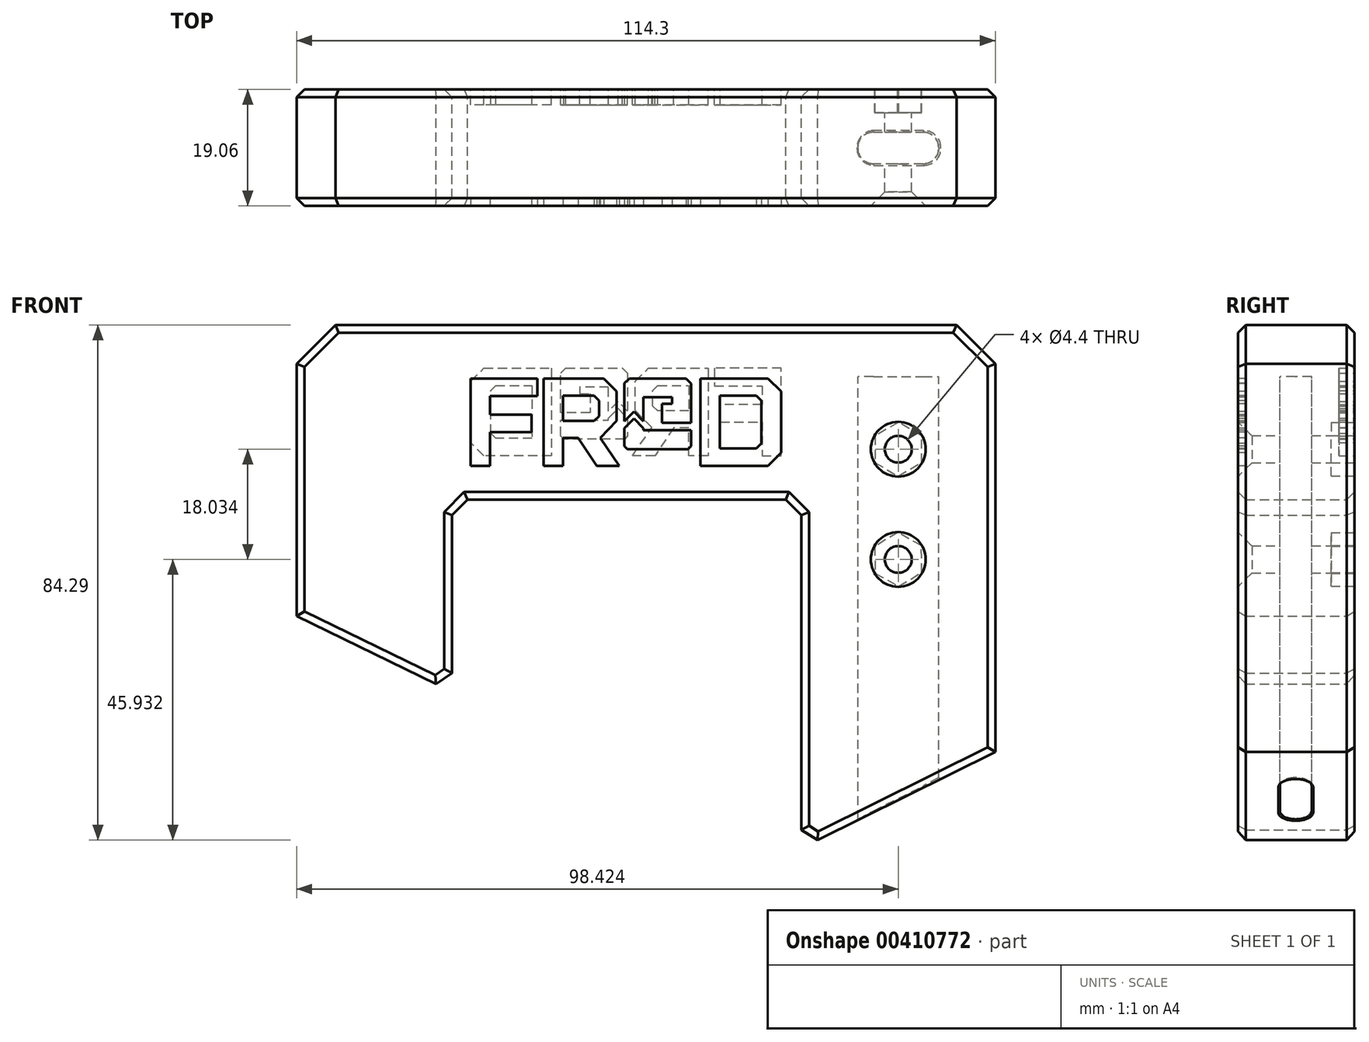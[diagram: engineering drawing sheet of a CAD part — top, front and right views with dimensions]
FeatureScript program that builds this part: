
annotation { "Feature Type Name" : "Feature", "Feature Type Description" : "" }
export const myFeature = defineFeature(function(context is Context, id is Id, definition is map)
    precondition{}
    {
        {
            var Q0;
            Q0=qCreatedBy(makeId("Front.planeOp"),FACE);
            var sketch = newSketch(context, id + "F0", { "sketchPlane" : qUnion([Q0])});
            skLineSegment(sketch, "E0", {"start": v(-47.53, 34.12) * mm, "end": v(54.07, 34.12) * mm});
            skLineSegment(sketch, "E1", {"start": v(60.42, 27.77) * mm, "end": v(60.42, -35.73) * mm});
            skLineSegment(sketch, "E2", {"start": v(60.42, -35.73) * mm, "end": v(31.37, -50.17) * mm});
            skLineSegment(sketch, "E3", {"start": v(28.67, -48.5) * mm, "end": v(28.67, 3) * mm});
            skLineSegment(sketch, "E4", {"start": v(26.13, 5.54) * mm, "end": v(-25.94, 5.54) * mm});
            skLineSegment(sketch, "E5", {"start": v(-28.48, 3) * mm, "end": v(-28.48, -22.82) * mm});
            skLineSegment(sketch, "E6", {"start": v(-31.1, -24.62) * mm, "end": v(-53.88, -13.5) * mm});
            skLineSegment(sketch, "E7", {"start": v(-53.88, -13.5) * mm, "end": v(-53.88, 27.77) * mm});
            skLineSegment(sketch, "E8", {"start": v(-31.1, -24.62) * mm, "end": v(-28.48, -22.82) * mm});
            skLineSegment(sketch, "E9", {"start": v(28.67, -48.5) * mm, "end": v(31.37, -50.17) * mm});
            skLineSegment(sketch, "E10", {"start": v(-53.88, 27.77) * mm, "end": v(-47.53, 34.12) * mm});
            skPoint(sketch, "E11.orphan", {"position": v(-53.88, 34.12) * mm});
            skLineSegment(sketch, "E12", {"start": v(54.07, 34.12) * mm, "end": v(60.42, 27.77) * mm});
            skPoint(sketch, "E13.orphan", {"position": v(60.42, 34.12) * mm});
            skLineSegment(sketch, "E14", {"start": v(-28.48, 3) * mm, "end": v(-25.94, 5.54) * mm});
            skPoint(sketch, "E15.orphan", {"position": v(-28.48, 5.54) * mm});
            skLineSegment(sketch, "E16", {"start": v(26.13, 5.54) * mm, "end": v(28.67, 3) * mm});
            skPoint(sketch, "E17.orphan", {"position": v(28.67, 5.54) * mm});
            skSolve(sketch);
        }
        {
            var Q0;
            Q0=makeQuery(id+"F0.imprint","IMPRINT",FACE,{"disambiguationData":[TD([[makeQuery(id+"F0.imprint","IMPRINT",EDGE,{"derivedFrom":sQuery(id+"F0.wireOp",EDGE,"E0")}),-1.0]])]});
            var Q1;
            Q1=makeQuery(id+"F0.imprint","IMPRINT",FACE,{"disambiguationData":[TD([[makeQuery(id+"F0.imprint","IMPRINT",EDGE,{"derivedFrom":sQuery(id+"F0.wireOp",EDGE,"ZEpFWphL-ozMd-Qc4S-y12z-fugVZn2PExex")}),1.0]])]});
            var Q2;
            Q2=makeQuery(id+"F0.imprint","IMPRINT",FACE,{"disambiguationData":[TD([[makeQuery(id+"F0.imprint","IMPRINT",EDGE,{"derivedFrom":sQuery(id+"F0.wireOp",EDGE,"a8f3txKb-fRa5-LG7a-W4z5-OOKFphKNCb56")}),1.0]])]});
            extrude(context, id + "F1", {"entities" : qUnion([Q0, Q1, Q2]), "depth" : 19.05 * mm, "offsetDistance" : 25.4 * mm, "symmetric" : true});
        }
        {
            var Q0;
            Q0=qCreatedBy(makeId("Top.planeOp"),FACE);
            var sketch = newSketch(context, id + "F2", { "sketchPlane" : qUnion([Q0])});
            skLineSegment(sketch, "E18.bottom", {"start": v(40.48, -2.67) * mm, "end": v(48.6, -2.67) * mm});
            skLineSegment(sketch, "E18.top", {"start": v(40.48, 2.54) * mm, "end": v(48.6, 2.54) * mm});
            skLineSegment(sketch, "E18.left", {"start": v(37.94, -0.13) * mm, "end": v(37.94, 0) * mm});
            skLineSegment(sketch, "E18.right", {"start": v(51.15, -0.13) * mm, "end": v(51.15, 0) * mm});
            skPoint(sketch, "E19.visualSharp", {"position": v(37.94, -2.67) * mm});
            skArc(sketch, "E19.filletArc", {"start": v(37.94, -0.13) * mm, "mid": v(38.68, -1.93) * mm, "end": v(40.48, -2.67) * mm});
            skPoint(sketch, "E20.visualSharp", {"position": v(37.94, 2.54) * mm});
            skArc(sketch, "E20.filletArc", {"start": v(40.48, 2.54) * mm, "mid": v(38.68, 1.8) * mm, "end": v(37.94, 0) * mm});
            skPoint(sketch, "E21.visualSharp", {"position": v(51.15, 2.54) * mm});
            skArc(sketch, "E21.filletArc", {"start": v(51.15, 0) * mm, "mid": v(50.4, 1.8) * mm, "end": v(48.6, 2.54) * mm});
            skPoint(sketch, "E22.visualSharp", {"position": v(51.15, -2.67) * mm});
            skArc(sketch, "E22.filletArc", {"start": v(48.6, -2.67) * mm, "mid": v(50.4, -1.93) * mm, "end": v(51.15, -0.13) * mm});
            skSolve(sketch);
        }
        {
            var Q0;
            Q0=makeQuery(id+"F2.imprint","IMPRINT",FACE,{"disambiguationData":[TD([[makeQuery(id+"F2.imprint","IMPRINT",EDGE,{"derivedFrom":sQuery(id+"F2.wireOp",EDGE,"E18.bottom")}),1.0]])]});
            extrude(context, id + "F3", {"entities" : qUnion([Q0]), "operationType" : NewBodyOperationType.REMOVE, "oppositeDirection" : true, "depth" : 59.33 * mm, "offsetDistance" : 25.4 * mm, "hasSecondDirection" : true, "secondDirectionOppositeDirection" : false, "secondDirectionDepth" : 25.65 * mm});
        }
        {
            var Q0;
            Q0=makeQuery(id+"F1.opExtrude","CAP_EDGE",EDGE,{"disambiguationData":[OSD([sQuery(id+"F0.wireOp",EDGE,"E0")])],"isStart":false});
            var Q1;
            Q1=makeQuery(id+"F1.opExtrude","CAP_EDGE",EDGE,{"disambiguationData":[OSD([sQuery(id+"F0.wireOp",EDGE,"E12")])],"isStart":false});
            var Q2;
            Q2=makeQuery(id+"F1.opExtrude","CAP_EDGE",EDGE,{"disambiguationData":[OSD([sQuery(id+"F0.wireOp",EDGE,"E1")])],"isStart":false});
            var Q3;
            Q3=makeQuery(id+"F1.opExtrude","CAP_EDGE",EDGE,{"disambiguationData":[OSD([sQuery(id+"F0.wireOp",EDGE,"E4")])],"isStart":false});
            var Q4;
            Q4=makeQuery(id+"F1.opExtrude","CAP_EDGE",EDGE,{"disambiguationData":[OSD([sQuery(id+"F0.wireOp",EDGE,"E16")])],"isStart":false});
            var Q5;
            Q5=makeQuery(id+"F1.opExtrude","CAP_EDGE",EDGE,{"disambiguationData":[OSD([sQuery(id+"F0.wireOp",EDGE,"E3")])],"isStart":false});
            var Q6;
            Q6=makeQuery(id+"F1.opExtrude","CAP_EDGE",EDGE,{"disambiguationData":[OSD([sQuery(id+"F0.wireOp",EDGE,"E9")])],"isStart":false});
            var Q7;
            Q7=makeQuery(id+"F1.opExtrude","CAP_EDGE",EDGE,{"disambiguationData":[OSD([sQuery(id+"F0.wireOp",EDGE,"E2")])],"isStart":false});
            var Q8;
            Q8=makeQuery(id+"F1.opExtrude","CAP_EDGE",EDGE,{"disambiguationData":[OSD([sQuery(id+"F0.wireOp",EDGE,"E1")])],"isStart":true});
            var Q9;
            Q9=makeQuery(id+"F1.opExtrude","CAP_EDGE",EDGE,{"disambiguationData":[OSD([sQuery(id+"F0.wireOp",EDGE,"E2")])],"isStart":true});
            var Q10;
            Q10=makeQuery(id+"F1.opExtrude","CAP_EDGE",EDGE,{"disambiguationData":[OSD([sQuery(id+"F0.wireOp",EDGE,"E12")])],"isStart":true});
            var Q11;
            Q11=makeQuery(id+"F1.opExtrude","CAP_EDGE",EDGE,{"disambiguationData":[OSD([sQuery(id+"F0.wireOp",EDGE,"E0")])],"isStart":true});
            var Q12;
            Q12=makeQuery(id+"F1.opExtrude","CAP_EDGE",EDGE,{"disambiguationData":[OSD([sQuery(id+"F0.wireOp",EDGE,"E3")])],"isStart":true});
            var Q13;
            Q13=makeQuery(id+"F1.opExtrude","CAP_EDGE",EDGE,{"disambiguationData":[OSD([sQuery(id+"F0.wireOp",EDGE,"E9")])],"isStart":true});
            var Q14;
            Q14=makeQuery(id+"F1.opExtrude","CAP_EDGE",EDGE,{"disambiguationData":[OSD([sQuery(id+"F0.wireOp",EDGE,"E16")])],"isStart":true});
            var Q15;
            Q15=makeQuery(id+"F1.opExtrude","CAP_EDGE",EDGE,{"disambiguationData":[OSD([sQuery(id+"F0.wireOp",EDGE,"E4")])],"isStart":true});
            var Q16;
            Q16=makeQuery(id+"F1.opExtrude","CAP_EDGE",EDGE,{"disambiguationData":[OSD([sQuery(id+"F0.wireOp",EDGE,"E14")])],"isStart":true});
            var Q17;
            Q17=makeQuery(id+"F1.opExtrude","CAP_EDGE",EDGE,{"disambiguationData":[OSD([sQuery(id+"F0.wireOp",EDGE,"E5")])],"isStart":true});
            var Q18;
            Q18=makeQuery(id+"F1.opExtrude","CAP_EDGE",EDGE,{"disambiguationData":[OSD([sQuery(id+"F0.wireOp",EDGE,"E8")])],"isStart":true});
            var Q19;
            Q19=makeQuery(id+"F1.opExtrude","CAP_EDGE",EDGE,{"disambiguationData":[OSD([sQuery(id+"F0.wireOp",EDGE,"E6")])],"isStart":true});
            var Q20;
            Q20=makeQuery(id+"F1.opExtrude","CAP_EDGE",EDGE,{"disambiguationData":[OSD([sQuery(id+"F0.wireOp",EDGE,"E7")])],"isStart":true});
            var Q21;
            Q21=makeQuery(id+"F1.opExtrude","CAP_EDGE",EDGE,{"disambiguationData":[OSD([sQuery(id+"F0.wireOp",EDGE,"E10")])],"isStart":true});
            var Q22;
            Q22=makeQuery(id+"F1.opExtrude","CAP_EDGE",EDGE,{"disambiguationData":[OSD([sQuery(id+"F0.wireOp",EDGE,"E10")])],"isStart":false});
            var Q23;
            Q23=makeQuery(id+"F1.opExtrude","CAP_EDGE",EDGE,{"disambiguationData":[OSD([sQuery(id+"F0.wireOp",EDGE,"E7")])],"isStart":false});
            var Q24;
            Q24=makeQuery(id+"F1.opExtrude","CAP_EDGE",EDGE,{"disambiguationData":[OSD([sQuery(id+"F0.wireOp",EDGE,"E6")])],"isStart":false});
            var Q25;
            Q25=makeQuery(id+"F1.opExtrude","CAP_EDGE",EDGE,{"disambiguationData":[OSD([sQuery(id+"F0.wireOp",EDGE,"E8")])],"isStart":false});
            var Q26;
            Q26=makeQuery(id+"F1.opExtrude","CAP_EDGE",EDGE,{"disambiguationData":[OSD([sQuery(id+"F0.wireOp",EDGE,"E5")])],"isStart":false});
            var Q27;
            Q27=makeQuery(id+"F1.opExtrude","CAP_EDGE",EDGE,{"disambiguationData":[OSD([sQuery(id+"F0.wireOp",EDGE,"E14")])],"isStart":false});
            chamfer(context, id + "F4", {"entities" : qUnion([Q0, Q1, Q2, Q3, Q4, Q5, Q6, Q7, Q8, Q9, Q10, Q11, Q12, Q13, Q14, Q15, Q16, Q17, Q18, Q19, Q20, Q21, Q22, Q23, Q24, Q25, Q26, Q27]), "width" : 1.27 * mm, "tangentPropagation" : true});
        }
        {
            var Q0;
            Q0=makeQuery(id+"F3.boolean.opBoolean","INTERSECT",EDGE,{"derivedFrom":[makeQuery(id+"F1.opExtrude","SWEPT_FACE",FACE,{"disambiguationData":[OSD([sQuery(id+"F0.wireOp",EDGE,"E2")])]}),makeQuery(id+"F3.opExtrude","SWEPT_FACE",FACE,{"disambiguationData":[OSD([sQuery(id+"F2.wireOp",EDGE,"E18.bottom")])]})]});
            chamfer(context, id + "F5", {"entities" : qUnion([Q0]), "width" : 0.25 * mm, "tangentPropagation" : true});
        }
        {
            var Q0;
            Q0=makeQuery(id+"F1.opExtrude","CAP_FACE",FACE,{"disambiguationData":[OSD([sQuery(id+"F0.wireOp",EDGE,"E0"),sQuery(id+"F0.wireOp",EDGE,"E1"),sQuery(id+"F0.wireOp",EDGE,"E2"),sQuery(id+"F0.wireOp",EDGE,"E3"),sQuery(id+"F0.wireOp",EDGE,"E4"),sQuery(id+"F0.wireOp",EDGE,"E5"),sQuery(id+"F0.wireOp",EDGE,"E6"),sQuery(id+"F0.wireOp",EDGE,"E7"),sQuery(id+"F0.wireOp",EDGE,"E8"),sQuery(id+"F0.wireOp",EDGE,"E9"),sQuery(id+"F0.wireOp",EDGE,"E10"),sQuery(id+"F0.wireOp",EDGE,"E12"),sQuery(id+"F0.wireOp",EDGE,"E14"),sQuery(id+"F0.wireOp",EDGE,"E16")])],"isStart":false});
            var sketch = newSketch(context, id + "F6", { "sketchPlane" : qUnion([Q0])});
            skCircle(sketch, "E23", {"center": v(44.54, 13.8) * mm, "radius": 1.9 * mm});
            skCircle(sketch, "E24", {"center": v(44.54, -4.24) * mm, "radius": 1.9 * mm});
            skSolve(sketch);
        }
        {
            var Q0;
            Q0=sQuery(id+"F6.wireOp",VERTEX,"E23.center");
            var Q1;
            Q1=sQuery(id+"F6.wireOp",VERTEX,"E24.center");
            var Q2;
            Q2=makeQuery(id+"F1.opExtrude","SWEPT_BODY",BODY,{"disambiguationData":[OSD([sQuery(id+"F0.wireOp",EDGE,"E0"),sQuery(id+"F0.wireOp",EDGE,"E1"),sQuery(id+"F0.wireOp",EDGE,"E2"),sQuery(id+"F0.wireOp",EDGE,"E3"),sQuery(id+"F0.wireOp",EDGE,"E4"),sQuery(id+"F0.wireOp",EDGE,"E5"),sQuery(id+"F0.wireOp",EDGE,"E6"),sQuery(id+"F0.wireOp",EDGE,"E7"),sQuery(id+"F0.wireOp",EDGE,"E8"),sQuery(id+"F0.wireOp",EDGE,"E9"),sQuery(id+"F0.wireOp",EDGE,"E10"),sQuery(id+"F0.wireOp",EDGE,"E12"),sQuery(id+"F0.wireOp",EDGE,"E14"),sQuery(id+"F0.wireOp",EDGE,"E16")])]});
            hole(context, id + "F7", {"style" : HoleStyle.C_SINK, "endStyle" : HoleEndStyle.THROUGH, "standardTappedOrClearance" : lookupTablePath({ "standard" : "ISO", "fit" : "Normal", "size" : "M4", "type" : "Clearance" }), "standardBlindInLast" : lookupTablePath({ "fit" : "Standard", "standard" : "ISO", "size" : "M4", "type" : "Clearance" }), "holeDiameter" : 4.4 * mm, "cSinkDiameter" : 8.96 * mm, "cSinkAngle" : 90 * degree, "isTappedThrough" : true, "tappedDepth" : 12.7 * mm, "tapClearance" : 3, "locations" : qUnion([Q0, Q1]), "scope" : qUnion([Q2]), "startStyle" : HoleStartStyle.PART});
        }
        {
            var Q0;
            Q0=makeQuery(id+"F1.opExtrude","CAP_FACE",FACE,{"disambiguationData":[OSD([sQuery(id+"F0.wireOp",EDGE,"E0"),sQuery(id+"F0.wireOp",EDGE,"E1"),sQuery(id+"F0.wireOp",EDGE,"E2"),sQuery(id+"F0.wireOp",EDGE,"E3"),sQuery(id+"F0.wireOp",EDGE,"E4"),sQuery(id+"F0.wireOp",EDGE,"E5"),sQuery(id+"F0.wireOp",EDGE,"E6"),sQuery(id+"F0.wireOp",EDGE,"E7"),sQuery(id+"F0.wireOp",EDGE,"E8"),sQuery(id+"F0.wireOp",EDGE,"E9"),sQuery(id+"F0.wireOp",EDGE,"E10"),sQuery(id+"F0.wireOp",EDGE,"E12"),sQuery(id+"F0.wireOp",EDGE,"E14"),sQuery(id+"F0.wireOp",EDGE,"E16")])],"isStart":true});
            var sketch = newSketch(context, id + "F8", { "sketchPlane" : qUnion([Q0])});
            skCircle(sketch, "E25.cCircle", {"center": v(-44.54, 13.8) * mm, "radius": 3.8 * mm, "construction": true});
            skLineSegment(sketch, "E25.0", {"start": v(-48.35, 11.6) * mm, "end": v(-48.35, 16) * mm});
            skLineSegment(sketch, "E25.1", {"start": v(-48.35, 16) * mm, "end": v(-44.54, 18.2) * mm});
            skLineSegment(sketch, "E25.2", {"start": v(-44.54, 18.2) * mm, "end": v(-40.73, 16) * mm});
            skLineSegment(sketch, "E25.3", {"start": v(-40.73, 16) * mm, "end": v(-40.73, 11.6) * mm});
            skLineSegment(sketch, "E25.4", {"start": v(-40.73, 11.6) * mm, "end": v(-44.54, 9.4) * mm});
            skLineSegment(sketch, "E25.5", {"start": v(-44.54, 9.4) * mm, "end": v(-48.35, 11.6) * mm});
            skPoint(sketch, "E25.0.midPoint", {"position": v(-48.35, 13.8) * mm});
            skCircle(sketch, "E26.cCircle", {"center": v(-44.54, -4.24) * mm, "radius": 3.81 * mm, "construction": true});
            skLineSegment(sketch, "E26.0", {"start": v(-48.31, -1.97) * mm, "end": v(-44.47, 0.16) * mm});
            skLineSegment(sketch, "E26.1", {"start": v(-44.47, 0.16) * mm, "end": v(-40.7, -2.1) * mm});
            skLineSegment(sketch, "E26.2", {"start": v(-40.7, -2.1) * mm, "end": v(-40.77, -6.5) * mm});
            skLineSegment(sketch, "E26.3", {"start": v(-40.77, -6.5) * mm, "end": v(-44.62, -8.64) * mm});
            skLineSegment(sketch, "E26.4", {"start": v(-44.62, -8.64) * mm, "end": v(-48.4, -6.37) * mm});
            skLineSegment(sketch, "E26.5", {"start": v(-48.4, -6.37) * mm, "end": v(-48.31, -1.97) * mm});
            skPoint(sketch, "E26.0.midPoint", {"position": v(-46.4, -0.9) * mm});
            skSolve(sketch);
        }
        {
            var Q0;
            Q0=makeQuery(id+"F8.imprint","IMPRINT",FACE,{"disambiguationData":[TD([[makeQuery(id+"F8.imprint","IMPRINT",EDGE,{"derivedFrom":sQuery(id+"F8.wireOp",EDGE,"E25.0")}),-1.0]])]});
            var Q1;
            Q1=makeQuery(id+"F8.imprint","IMPRINT",FACE,{"disambiguationData":[TD([[makeQuery(id+"F8.imprint","IMPRINT",EDGE,{"derivedFrom":sQuery(id+"F8.wireOp",EDGE,"E26.0")}),-1.0]])]});
            extrude(context, id + "F9", {"entities" : qUnion([Q0, Q1]), "operationType" : NewBodyOperationType.REMOVE, "oppositeDirection" : true, "depth" : 3.8 * mm, "offsetDistance" : 25.4 * mm});
        }
        {
            var Q0;
            Q0=makeQuery(id+"F1.opExtrude","CAP_FACE",FACE,{"disambiguationData":[OSD([sQuery(id+"F0.wireOp",EDGE,"E0"),sQuery(id+"F0.wireOp",EDGE,"E1"),sQuery(id+"F0.wireOp",EDGE,"E2"),sQuery(id+"F0.wireOp",EDGE,"E3"),sQuery(id+"F0.wireOp",EDGE,"E4"),sQuery(id+"F0.wireOp",EDGE,"E5"),sQuery(id+"F0.wireOp",EDGE,"E6"),sQuery(id+"F0.wireOp",EDGE,"E7"),sQuery(id+"F0.wireOp",EDGE,"E8"),sQuery(id+"F0.wireOp",EDGE,"E9"),sQuery(id+"F0.wireOp",EDGE,"E10"),sQuery(id+"F0.wireOp",EDGE,"E12"),sQuery(id+"F0.wireOp",EDGE,"E14"),sQuery(id+"F0.wireOp",EDGE,"E16")])],"isStart":false});
            var sketch = newSketch(context, id + "F10", { "sketchPlane" : qUnion([Q0])});
            skLineSegment(sketch, "E27", {"start": v(-25.4, 25.38) * mm, "end": v(-14.5, 25.38) * mm});
            skLineSegment(sketch, "E28", {"start": v(-14.5, 25.38) * mm, "end": v(-14.5, 22.52) * mm});
            skLineSegment(sketch, "E29", {"start": v(-14.5, 22.52) * mm, "end": v(-22.25, 22.52) * mm});
            skLineSegment(sketch, "E30", {"start": v(-22.25, 22.52) * mm, "end": v(-22.25, 19.47) * mm});
            skLineSegment(sketch, "E31", {"start": v(-22.25, 19.47) * mm, "end": v(-15.42, 19.47) * mm});
            skLineSegment(sketch, "E32", {"start": v(-15.42, 19.47) * mm, "end": v(-15.42, 16.6) * mm});
            skLineSegment(sketch, "E33", {"start": v(-15.42, 16.6) * mm, "end": v(-22.25, 16.6) * mm});
            skLineSegment(sketch, "E34", {"start": v(-22.25, 16.6) * mm, "end": v(-22.25, 11.06) * mm});
            skLineSegment(sketch, "E35", {"start": v(-22.25, 11.06) * mm, "end": v(-25.4, 11.06) * mm});
            skLineSegment(sketch, "E36", {"start": v(-25.4, 11.06) * mm, "end": v(-25.4, 25.38) * mm});
            skLineSegment(sketch, "E37", {"start": v(2.84, 16.91) * mm, "end": v(2.84, 17.23) * mm});
            skLineSegment(sketch, "E38", {"start": v(2.84, 17.23) * mm, "end": v(1.3, 18.8) * mm});
            skLineSegment(sketch, "E39", {"start": v(1.3, 18.8) * mm, "end": v(-0.26, 17.23) * mm});
            skLineSegment(sketch, "E40", {"start": v(-0.26, 17.23) * mm, "end": v(-0.26, 16.91) * mm});
            skLineSegment(sketch, "E41", {"start": v(-0.26, 16.91) * mm, "end": v(-0.26, 14.47) * mm});
            skLineSegment(sketch, "E42", {"start": v(-0.26, 14.47) * mm, "end": v(-0.26, 14.3) * mm});
            skLineSegment(sketch, "E43", {"start": v(-0.26, 14.3) * mm, "end": v(0.23, 13.81) * mm});
            skLineSegment(sketch, "E44", {"start": v(0.23, 13.81) * mm, "end": v(10.17, 13.81) * mm});
            skLineSegment(sketch, "E45", {"start": v(10.17, 13.81) * mm, "end": v(10.66, 14.3) * mm});
            skLineSegment(sketch, "E46", {"start": v(10.66, 14.3) * mm, "end": v(10.66, 16.91) * mm});
            skLineSegment(sketch, "E47", {"start": v(10.66, 16.91) * mm, "end": v(2.84, 16.91) * mm});
            skLineSegment(sketch, "E48", {"start": v(-0.26, 24.56) * mm, "end": v(-0.26, 22.28) * mm});
            skLineSegment(sketch, "E49", {"start": v(-0.26, 22.28) * mm, "end": v(-0.26, 18.38) * mm});
            skLineSegment(sketch, "E50", {"start": v(-0.26, 18.38) * mm, "end": v(1.3, 19.94) * mm});
            skLineSegment(sketch, "E51", {"start": v(1.3, 19.94) * mm, "end": v(2.84, 18.38) * mm});
            skLineSegment(sketch, "E52", {"start": v(2.84, 18.38) * mm, "end": v(2.84, 22.28) * mm});
            skLineSegment(sketch, "E53", {"start": v(2.84, 22.28) * mm, "end": v(7.56, 22.28) * mm});
            skLineSegment(sketch, "E54", {"start": v(7.56, 22.28) * mm, "end": v(7.56, 21.2) * mm});
            skLineSegment(sketch, "E55", {"start": v(7.56, 21.2) * mm, "end": v(5.87, 21.2) * mm});
            skLineSegment(sketch, "E56", {"start": v(5.87, 21.2) * mm, "end": v(5.87, 18.1) * mm});
            skLineSegment(sketch, "E57", {"start": v(5.87, 18.1) * mm, "end": v(10.66, 18.1) * mm});
            skLineSegment(sketch, "E58", {"start": v(10.66, 18.1) * mm, "end": v(10.66, 19.48) * mm});
            skLineSegment(sketch, "E59", {"start": v(10.66, 19.48) * mm, "end": v(10.66, 21.2) * mm});
            skLineSegment(sketch, "E60", {"start": v(10.66, 21.2) * mm, "end": v(10.66, 22.28) * mm});
            skLineSegment(sketch, "E61", {"start": v(10.66, 22.28) * mm, "end": v(10.66, 24.56) * mm});
            skLineSegment(sketch, "E62", {"start": v(10.66, 24.56) * mm, "end": v(9.84, 25.38) * mm});
            skLineSegment(sketch, "E63", {"start": v(9.84, 25.38) * mm, "end": v(2.84, 25.38) * mm});
            skLineSegment(sketch, "E64", {"start": v(2.84, 25.38) * mm, "end": v(0.56, 25.38) * mm});
            skLineSegment(sketch, "E65", {"start": v(0.56, 25.38) * mm, "end": v(-0.26, 24.56) * mm});
            skLineSegment(sketch, "E66", {"start": v(-4.22, 15.66) * mm, "end": v(-1.51, 18.46) * mm});
            skLineSegment(sketch, "E67", {"start": v(-1.51, 18.46) * mm, "end": v(-1.51, 23.23) * mm});
            skLineSegment(sketch, "E68", {"start": v(-1.51, 23.23) * mm, "end": v(-3.66, 25.38) * mm});
            skLineSegment(sketch, "E69", {"start": v(-3.66, 25.38) * mm, "end": v(-13.45, 25.38) * mm});
            skLineSegment(sketch, "E70", {"start": v(-13.45, 25.38) * mm, "end": v(-13.45, 11.06) * mm});
            skLineSegment(sketch, "E71", {"start": v(-13.45, 11.06) * mm, "end": v(-10.3, 11.06) * mm});
            skLineSegment(sketch, "E72", {"start": v(-10.3, 11.06) * mm, "end": v(-10.3, 15.64) * mm});
            skLineSegment(sketch, "E73", {"start": v(-10.3, 15.64) * mm, "end": v(-7.82, 15.64) * mm});
            skLineSegment(sketch, "E74", {"start": v(-7.82, 15.64) * mm, "end": v(-4.75, 11.06) * mm});
            skLineSegment(sketch, "E75", {"start": v(-4.75, 11.06) * mm, "end": v(-1.07, 11.06) * mm});
            skLineSegment(sketch, "E76", {"start": v(-1.07, 11.06) * mm, "end": v(-4.22, 15.66) * mm});
            skLineSegment(sketch, "E77", {"start": v(17.94, 11.06) * mm, "end": v(23.17, 11.06) * mm});
            skLineSegment(sketch, "E78", {"start": v(23.17, 11.06) * mm, "end": v(23.25, 11.06) * mm});
            skLineSegment(sketch, "E79", {"start": v(23.25, 11.06) * mm, "end": v(25.4, 13.2) * mm});
            skLineSegment(sketch, "E80", {"start": v(25.4, 13.2) * mm, "end": v(25.4, 17.98) * mm});
            skLineSegment(sketch, "E81", {"start": v(25.4, 17.98) * mm, "end": v(25.4, 18.46) * mm});
            skLineSegment(sketch, "E82", {"start": v(25.4, 18.46) * mm, "end": v(25.4, 23.23) * mm});
            skLineSegment(sketch, "E83", {"start": v(25.4, 23.23) * mm, "end": v(23.25, 25.38) * mm});
            skLineSegment(sketch, "E84", {"start": v(23.25, 25.38) * mm, "end": v(23.17, 25.38) * mm});
            skLineSegment(sketch, "E85", {"start": v(23.17, 25.38) * mm, "end": v(17.94, 25.38) * mm});
            skLineSegment(sketch, "E86", {"start": v(17.94, 25.38) * mm, "end": v(17.79, 25.38) * mm});
            skLineSegment(sketch, "E87", {"start": v(17.79, 25.38) * mm, "end": v(12.2, 25.38) * mm});
            skLineSegment(sketch, "E88", {"start": v(12.2, 25.38) * mm, "end": v(12.2, 11.06) * mm});
            skLineSegment(sketch, "E89", {"start": v(12.2, 11.06) * mm, "end": v(17.79, 11.06) * mm});
            skLineSegment(sketch, "E90", {"start": v(17.79, 11.06) * mm, "end": v(17.94, 11.06) * mm});
            skLineSegment(sketch, "E91", {"start": v(-5.22, 18.4) * mm, "end": v(-4.4, 19.2) * mm});
            skLineSegment(sketch, "E92", {"start": v(-4.4, 19.2) * mm, "end": v(-4.4, 21.72) * mm});
            skLineSegment(sketch, "E93", {"start": v(-4.4, 21.72) * mm, "end": v(-5.22, 22.54) * mm});
            skLineSegment(sketch, "E94", {"start": v(-5.22, 22.54) * mm, "end": v(-10.3, 22.54) * mm});
            skLineSegment(sketch, "E95", {"start": v(-10.3, 22.54) * mm, "end": v(-10.3, 18.4) * mm});
            skLineSegment(sketch, "E96", {"start": v(-10.3, 18.4) * mm, "end": v(-5.22, 18.4) * mm});
            skLineSegment(sketch, "E97", {"start": v(21.3, 13.9) * mm, "end": v(22.13, 14.72) * mm});
            skLineSegment(sketch, "E98", {"start": v(22.13, 14.72) * mm, "end": v(22.13, 21.72) * mm});
            skLineSegment(sketch, "E99", {"start": v(22.13, 21.72) * mm, "end": v(21.3, 22.54) * mm});
            skLineSegment(sketch, "E100", {"start": v(21.3, 22.54) * mm, "end": v(15.35, 22.54) * mm});
            skLineSegment(sketch, "E101", {"start": v(15.35, 22.54) * mm, "end": v(15.35, 13.9) * mm});
            skLineSegment(sketch, "E102", {"start": v(15.35, 13.9) * mm, "end": v(21.3, 13.9) * mm});
            skSolve(sketch);
        }
        {
            var Q0;
            Q0=makeQuery(id+"F10.imprint","IMPRINT",FACE,{"disambiguationData":[TD([[makeQuery(id+"F10.imprint","IMPRINT",EDGE,{"derivedFrom":sQuery(id+"F10.wireOp",EDGE,"E27")}),-1.0]])]});
            var Q1;
            Q1=makeQuery(id+"F10.imprint","IMPRINT",FACE,{"disambiguationData":[TD([[makeQuery(id+"F10.imprint","IMPRINT",EDGE,{"derivedFrom":sQuery(id+"F10.wireOp",EDGE,"E66")}),1.0]])]});
            var Q2;
            Q2=makeQuery(id+"F10.imprint","IMPRINT",FACE,{"disambiguationData":[TD([[makeQuery(id+"F10.imprint","IMPRINT",EDGE,{"derivedFrom":sQuery(id+"F10.wireOp",EDGE,"E48")}),1.0]])]});
            var Q3;
            Q3=makeQuery(id+"F10.imprint","IMPRINT",FACE,{"disambiguationData":[TD([[makeQuery(id+"F10.imprint","IMPRINT",EDGE,{"derivedFrom":sQuery(id+"F10.wireOp",EDGE,"E37")}),1.0]])]});
            var Q4;
            Q4=makeQuery(id+"F10.imprint","IMPRINT",FACE,{"disambiguationData":[TD([[makeQuery(id+"F10.imprint","IMPRINT",EDGE,{"derivedFrom":sQuery(id+"F10.wireOp",EDGE,"E77")}),1.0]])]});
            extrude(context, id + "F11", {"entities" : qUnion([Q0, Q1, Q2, Q3, Q4]), "operationType" : NewBodyOperationType.REMOVE, "oppositeDirection" : true, "depth" : 1.27 * mm, "offsetDistance" : 25.4 * mm});
        }
        {
            var Q0;
            Q0=makeQuery(id+"F1.opExtrude","CAP_FACE",FACE,{"disambiguationData":[OSD([sQuery(id+"F0.wireOp",EDGE,"E0"),sQuery(id+"F0.wireOp",EDGE,"E1"),sQuery(id+"F0.wireOp",EDGE,"E2"),sQuery(id+"F0.wireOp",EDGE,"E3"),sQuery(id+"F0.wireOp",EDGE,"E4"),sQuery(id+"F0.wireOp",EDGE,"E5"),sQuery(id+"F0.wireOp",EDGE,"E6"),sQuery(id+"F0.wireOp",EDGE,"E7"),sQuery(id+"F0.wireOp",EDGE,"E8"),sQuery(id+"F0.wireOp",EDGE,"E9"),sQuery(id+"F0.wireOp",EDGE,"E10"),sQuery(id+"F0.wireOp",EDGE,"E12"),sQuery(id+"F0.wireOp",EDGE,"E14"),sQuery(id+"F0.wireOp",EDGE,"E16")])],"isStart":true});
            var sketch = newSketch(context, id + "F12", { "sketchPlane" : qUnion([Q0])});
            skLineSegment(sketch, "E103", {"start": v(-25.4, 27.04) * mm, "end": v(-14.5, 27.04) * mm});
            skLineSegment(sketch, "E104", {"start": v(-14.5, 27.04) * mm, "end": v(-14.5, 24.18) * mm});
            skLineSegment(sketch, "E105", {"start": v(-14.5, 24.18) * mm, "end": v(-22.25, 24.18) * mm});
            skLineSegment(sketch, "E106", {"start": v(-22.25, 24.18) * mm, "end": v(-22.25, 21.13) * mm});
            skLineSegment(sketch, "E107", {"start": v(-22.25, 21.13) * mm, "end": v(-15.42, 21.13) * mm});
            skLineSegment(sketch, "E108", {"start": v(-15.42, 21.13) * mm, "end": v(-15.42, 18.27) * mm});
            skLineSegment(sketch, "E109", {"start": v(-15.42, 18.27) * mm, "end": v(-22.25, 18.27) * mm});
            skLineSegment(sketch, "E110", {"start": v(-22.25, 18.27) * mm, "end": v(-22.25, 12.72) * mm});
            skLineSegment(sketch, "E111", {"start": v(-22.25, 12.72) * mm, "end": v(-25.4, 12.72) * mm});
            skLineSegment(sketch, "E112", {"start": v(-25.4, 12.72) * mm, "end": v(-25.4, 27.04) * mm});
            skLineSegment(sketch, "E113", {"start": v(2.84, 18.58) * mm, "end": v(2.84, 18.9) * mm});
            skLineSegment(sketch, "E114", {"start": v(2.84, 18.9) * mm, "end": v(1.3, 20.46) * mm});
            skLineSegment(sketch, "E115", {"start": v(1.3, 20.46) * mm, "end": v(-0.26, 18.9) * mm});
            skLineSegment(sketch, "E116", {"start": v(-0.26, 18.9) * mm, "end": v(-0.26, 18.58) * mm});
            skLineSegment(sketch, "E117", {"start": v(-0.26, 18.58) * mm, "end": v(-0.26, 16.13) * mm});
            skLineSegment(sketch, "E118", {"start": v(-0.26, 16.13) * mm, "end": v(-0.26, 15.96) * mm});
            skLineSegment(sketch, "E119", {"start": v(-0.26, 15.96) * mm, "end": v(0.23, 15.48) * mm});
            skLineSegment(sketch, "E120", {"start": v(0.23, 15.48) * mm, "end": v(10.17, 15.48) * mm});
            skLineSegment(sketch, "E121", {"start": v(10.17, 15.48) * mm, "end": v(10.66, 15.97) * mm});
            skLineSegment(sketch, "E122", {"start": v(10.66, 15.97) * mm, "end": v(10.66, 18.58) * mm});
            skLineSegment(sketch, "E123", {"start": v(10.66, 18.58) * mm, "end": v(2.84, 18.58) * mm});
            skLineSegment(sketch, "E124", {"start": v(-0.26, 26.23) * mm, "end": v(-0.26, 23.94) * mm});
            skLineSegment(sketch, "E125", {"start": v(-0.26, 23.94) * mm, "end": v(-0.26, 20.04) * mm});
            skLineSegment(sketch, "E126", {"start": v(-0.26, 20.04) * mm, "end": v(1.3, 21.6) * mm});
            skLineSegment(sketch, "E127", {"start": v(1.3, 21.6) * mm, "end": v(2.84, 20.04) * mm});
            skLineSegment(sketch, "E128", {"start": v(2.84, 20.04) * mm, "end": v(2.84, 23.94) * mm});
            skLineSegment(sketch, "E129", {"start": v(2.84, 23.94) * mm, "end": v(7.56, 23.94) * mm});
            skLineSegment(sketch, "E130", {"start": v(7.56, 23.94) * mm, "end": v(7.56, 22.87) * mm});
            skLineSegment(sketch, "E131", {"start": v(7.56, 22.87) * mm, "end": v(5.87, 22.87) * mm});
            skLineSegment(sketch, "E132", {"start": v(5.87, 22.87) * mm, "end": v(5.87, 19.77) * mm});
            skLineSegment(sketch, "E133", {"start": v(5.87, 19.77) * mm, "end": v(10.66, 19.77) * mm});
            skLineSegment(sketch, "E134", {"start": v(10.66, 19.77) * mm, "end": v(10.66, 21.15) * mm});
            skLineSegment(sketch, "E135", {"start": v(10.66, 21.15) * mm, "end": v(10.66, 22.87) * mm});
            skLineSegment(sketch, "E136", {"start": v(10.66, 22.87) * mm, "end": v(10.66, 23.94) * mm});
            skLineSegment(sketch, "E137", {"start": v(10.66, 23.94) * mm, "end": v(10.66, 26.22) * mm});
            skLineSegment(sketch, "E138", {"start": v(10.66, 26.22) * mm, "end": v(9.84, 27.04) * mm});
            skLineSegment(sketch, "E139", {"start": v(9.84, 27.04) * mm, "end": v(2.84, 27.04) * mm});
            skLineSegment(sketch, "E140", {"start": v(2.84, 27.04) * mm, "end": v(0.56, 27.04) * mm});
            skLineSegment(sketch, "E141", {"start": v(0.56, 27.04) * mm, "end": v(-0.26, 26.23) * mm});
            skLineSegment(sketch, "E142", {"start": v(-4.22, 17.33) * mm, "end": v(-1.51, 20.13) * mm});
            skLineSegment(sketch, "E143", {"start": v(-1.51, 20.13) * mm, "end": v(-1.51, 24.9) * mm});
            skLineSegment(sketch, "E144", {"start": v(-1.51, 24.9) * mm, "end": v(-3.66, 27.04) * mm});
            skLineSegment(sketch, "E145", {"start": v(-3.66, 27.04) * mm, "end": v(-13.45, 27.04) * mm});
            skLineSegment(sketch, "E146", {"start": v(-13.45, 27.04) * mm, "end": v(-13.45, 12.72) * mm});
            skLineSegment(sketch, "E147", {"start": v(-13.45, 12.72) * mm, "end": v(-10.3, 12.72) * mm});
            skLineSegment(sketch, "E148", {"start": v(-10.3, 12.72) * mm, "end": v(-10.3, 17.3) * mm});
            skLineSegment(sketch, "E149", {"start": v(-10.3, 17.3) * mm, "end": v(-7.82, 17.3) * mm});
            skLineSegment(sketch, "E150", {"start": v(-7.82, 17.3) * mm, "end": v(-4.75, 12.72) * mm});
            skLineSegment(sketch, "E151", {"start": v(-4.75, 12.72) * mm, "end": v(-1.07, 12.72) * mm});
            skLineSegment(sketch, "E152", {"start": v(-1.07, 12.72) * mm, "end": v(-4.22, 17.33) * mm});
            skLineSegment(sketch, "E153", {"start": v(17.94, 12.72) * mm, "end": v(23.17, 12.72) * mm});
            skLineSegment(sketch, "E154", {"start": v(23.17, 12.72) * mm, "end": v(23.25, 12.72) * mm});
            skLineSegment(sketch, "E155", {"start": v(23.25, 12.72) * mm, "end": v(25.4, 14.87) * mm});
            skLineSegment(sketch, "E156", {"start": v(25.4, 14.87) * mm, "end": v(25.4, 19.64) * mm});
            skLineSegment(sketch, "E157", {"start": v(25.4, 19.64) * mm, "end": v(25.4, 20.13) * mm});
            skLineSegment(sketch, "E158", {"start": v(25.4, 20.13) * mm, "end": v(25.4, 24.9) * mm});
            skLineSegment(sketch, "E159", {"start": v(25.4, 24.9) * mm, "end": v(23.25, 27.04) * mm});
            skLineSegment(sketch, "E160", {"start": v(23.25, 27.04) * mm, "end": v(23.17, 27.04) * mm});
            skLineSegment(sketch, "E161", {"start": v(23.17, 27.04) * mm, "end": v(17.94, 27.04) * mm});
            skLineSegment(sketch, "E162", {"start": v(17.94, 27.04) * mm, "end": v(17.79, 27.04) * mm});
            skLineSegment(sketch, "E163", {"start": v(17.79, 27.04) * mm, "end": v(12.2, 27.04) * mm});
            skLineSegment(sketch, "E164", {"start": v(12.2, 27.04) * mm, "end": v(12.2, 12.72) * mm});
            skLineSegment(sketch, "E165", {"start": v(12.2, 12.72) * mm, "end": v(17.79, 12.72) * mm});
            skLineSegment(sketch, "E166", {"start": v(17.79, 12.72) * mm, "end": v(17.94, 12.72) * mm});
            skLineSegment(sketch, "E167", {"start": v(-5.22, 20.07) * mm, "end": v(-4.4, 20.87) * mm});
            skLineSegment(sketch, "E168", {"start": v(-4.4, 20.87) * mm, "end": v(-4.4, 23.39) * mm});
            skLineSegment(sketch, "E169", {"start": v(-4.4, 23.39) * mm, "end": v(-5.22, 24.2) * mm});
            skLineSegment(sketch, "E170", {"start": v(-5.22, 24.2) * mm, "end": v(-10.3, 24.2) * mm});
            skLineSegment(sketch, "E171", {"start": v(-10.3, 24.2) * mm, "end": v(-10.3, 20.07) * mm});
            skLineSegment(sketch, "E172", {"start": v(-10.3, 20.07) * mm, "end": v(-5.22, 20.07) * mm});
            skLineSegment(sketch, "E173", {"start": v(21.3, 15.57) * mm, "end": v(22.13, 16.39) * mm});
            skLineSegment(sketch, "E174", {"start": v(22.13, 16.39) * mm, "end": v(22.13, 23.39) * mm});
            skLineSegment(sketch, "E175", {"start": v(22.13, 23.39) * mm, "end": v(21.3, 24.2) * mm});
            skLineSegment(sketch, "E176", {"start": v(21.3, 24.2) * mm, "end": v(15.35, 24.2) * mm});
            skLineSegment(sketch, "E177", {"start": v(15.35, 24.2) * mm, "end": v(15.35, 15.57) * mm});
            skLineSegment(sketch, "E178", {"start": v(15.35, 15.57) * mm, "end": v(21.3, 15.57) * mm});
            skSolve(sketch);
        }
        {
            var Q0;
            Q0=makeQuery(id+"F12.imprint","IMPRINT",FACE,{"disambiguationData":[TD([[makeQuery(id+"F12.imprint","IMPRINT",EDGE,{"derivedFrom":sQuery(id+"F12.wireOp",EDGE,"E113")}),1.0]])]});
            var Q1;
            Q1=makeQuery(id+"F12.imprint","IMPRINT",FACE,{"disambiguationData":[TD([[makeQuery(id+"F12.imprint","IMPRINT",EDGE,{"derivedFrom":sQuery(id+"F12.wireOp",EDGE,"E124")}),1.0]])]});
            var Q2;
            Q2=makeQuery(id+"F12.imprint","IMPRINT",FACE,{"disambiguationData":[TD([[makeQuery(id+"F12.imprint","IMPRINT",EDGE,{"derivedFrom":sQuery(id+"F12.wireOp",EDGE,"E142")}),1.0]])]});
            var Q3;
            Q3=makeQuery(id+"F12.imprint","IMPRINT",FACE,{"disambiguationData":[TD([[makeQuery(id+"F12.imprint","IMPRINT",EDGE,{"derivedFrom":sQuery(id+"F12.wireOp",EDGE,"E153")}),1.0]])]});
            var Q4;
            Q4=makeQuery(id+"F12.imprint","IMPRINT",FACE,{"disambiguationData":[TD([[makeQuery(id+"F12.imprint","IMPRINT",EDGE,{"derivedFrom":sQuery(id+"F12.wireOp",EDGE,"E103")}),-1.0]])]});
            extrude(context, id + "F13", {"entities" : qUnion([Q0, Q1, Q2, Q3, Q4]), "operationType" : NewBodyOperationType.REMOVE, "oppositeDirection" : true, "depth" : 2.54 * mm, "offsetDistance" : 25.4 * mm});
        }
    });
